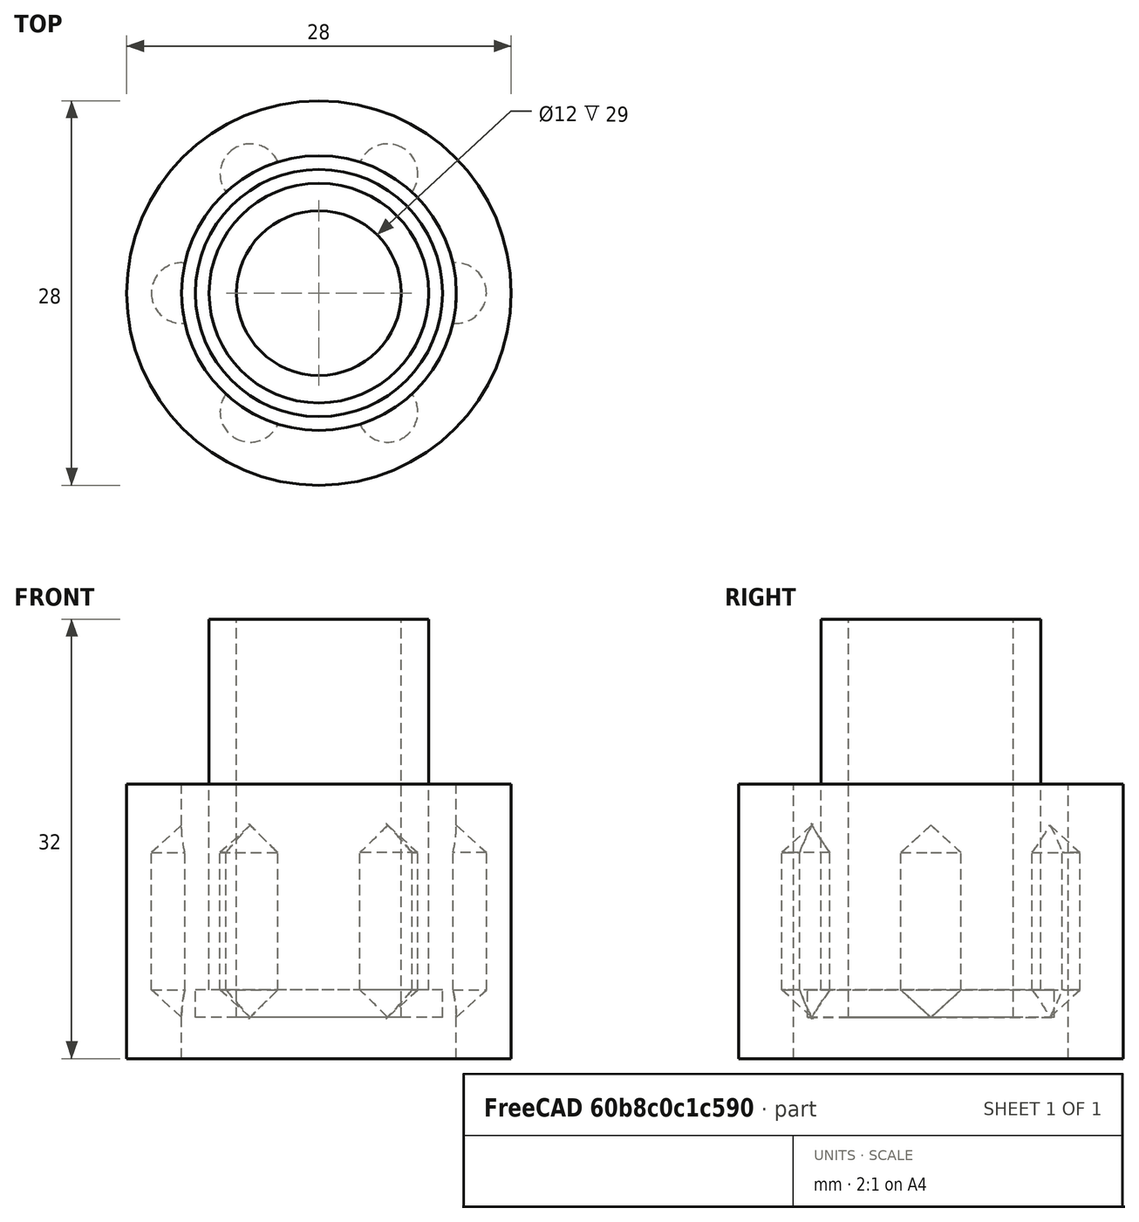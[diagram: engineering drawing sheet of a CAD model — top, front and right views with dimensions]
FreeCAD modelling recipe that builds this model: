
FCSTD DOCUMENT  (FreeCAD 0.16R6703 (Git))
Label: bearing-test
License: All rights reserved
LicenseURL: http://en.wikipedia.org/wiki/All_rights_reserved
objects: Part::Cut×8, Part::Cylinder×6, Part::Feature×4, Part::MultiFuse×3, Part::Cone×2, Part::Mirroring×1
note: 24 computed .brp shape members not serialized (recipe doc carries the construction recipe); baked Part::Feature solids carry a one-line shape summary decoded from their .brp

FEATURE [Part::Cylinder] Cylinder
  Angle = 360
  Height = 10
  Radius = 2.2
FEATURE [Part::Cone] Cone
  Angle = 360
  Height = 2
  Placement = pos=(0,0,-2) rot=(0,0,1;0rad)
  Radius1 = 0
  Radius2 = 2.2
FEATURE [Part::Cone] Cone001
  Angle = 360
  Height = 2
  Placement = pos=(0,0,-2) rot=(0,0,1;0rad)
  Radius1 = 0
  Radius2 = 2.2
FEATURE [Part::Mirroring] Part__Mirroring  label="Cone001 (Mirror #1)"
  Base = (0,0,0)
  Normal = (0,0,1)
  Placement = pos=(0,0,10) rot=(0,0,1;0rad)
  Source = -> Cone001
FEATURE [Part::MultiFuse] Fusion  label="bearing-cavity"
  Placement = pos=(10,0,0) rot=(0,0,1;0rad)
  Shapes = -> [Cylinder,Cone,Part__Mirroring]
FEATURE [Part::Cylinder] Cylinder001
  Angle = 360
  Height = 32
  Placement = pos=(0,0,-11) rot=(0,0,1;0rad)
  Radius = 10
FEATURE [Part::Feature] Fusion001
  Placement = pos=(5,8.66025,0) rot=(0,0,1;1.0472rad)
  shape: bbox 4.4 x 4.4 x 14 mm, 3 faces (baked)
FEATURE [Part::Feature] Fusion002
  Placement = pos=(-5,8.66025,0) rot=(0,0,1;2.0944rad)
  shape: bbox 4.4 x 4.4 x 14 mm, 3 faces (baked)
FEATURE [Part::Feature] Fusion003
  Placement = pos=(-10,0,0) rot=(0,0,1;3.14159rad)
  shape: bbox 4.4 x 4.4 x 14 mm, 3 faces (baked)
FEATURE [Part::Feature] Fusion004
  Placement = pos=(-5,-8.66025,0) rot=(0,0,1;4.18879rad)
  shape: bbox 4.4 x 4.4 x 14 mm, 3 faces (baked)
FEATURE [Part::Cylinder] Cylinder002
  Angle = 360
  Height = 20
  Placement = pos=(0,0,-5) rot=(0,0,1;0rad)
  Radius = 14
FEATURE [Part::Cut] Cut
  Base = -> Cylinder002
  Tool = -> Cylinder001
FEATURE [Part::Cut] Cut001
  Base = -> Cut
  Tool = -> Fusion
FEATURE [Part::Cut] Cut002
  Base = -> Cut001
  Tool = -> Fusion004
FEATURE [Part::Cut] Cut003
  Base = -> Cut002
  Tool = -> Fusion003
FEATURE [Part::Cut] Cut004
  Base = -> Cut003
  Tool = -> Fusion002
FEATURE [Part::Cut] Cut005
  Base = -> Cut004
  Tool = -> Fusion001
FEATURE [Part::MultiFuse] Fusion006  label="bearing-cavity001"
  Placement = pos=(5,-8.66025,0) rot=(0,0,-1;1.0472rad)
  Shapes = -> [Cylinder,Cone,Part__Mirroring]
FEATURE [Part::Cut] Cut006
  Base = -> Cut005
  Tool = -> Fusion006
FEATURE [Part::Cylinder] Cylinder003
  Angle = 360
  Height = 27
  Radius = 8
FEATURE [Part::Cylinder] Cylinder004
  Angle = 360
  Height = 2
  Placement = pos=(0,0,-2) rot=(0,0,1;0rad)
  Radius = 9
FEATURE [Part::MultiFuse] Fusion007
  Shapes = -> [Cylinder003,Cylinder004]
FEATURE [Part::Cylinder] Cylinder005
  Angle = 360
  Height = 50
  Placement = pos=(0,0,-15) rot=(0,0,1;0rad)
  Radius = 6
FEATURE [Part::Cut] Cut007
  Base = -> Fusion007
  Tool = -> Cylinder005
